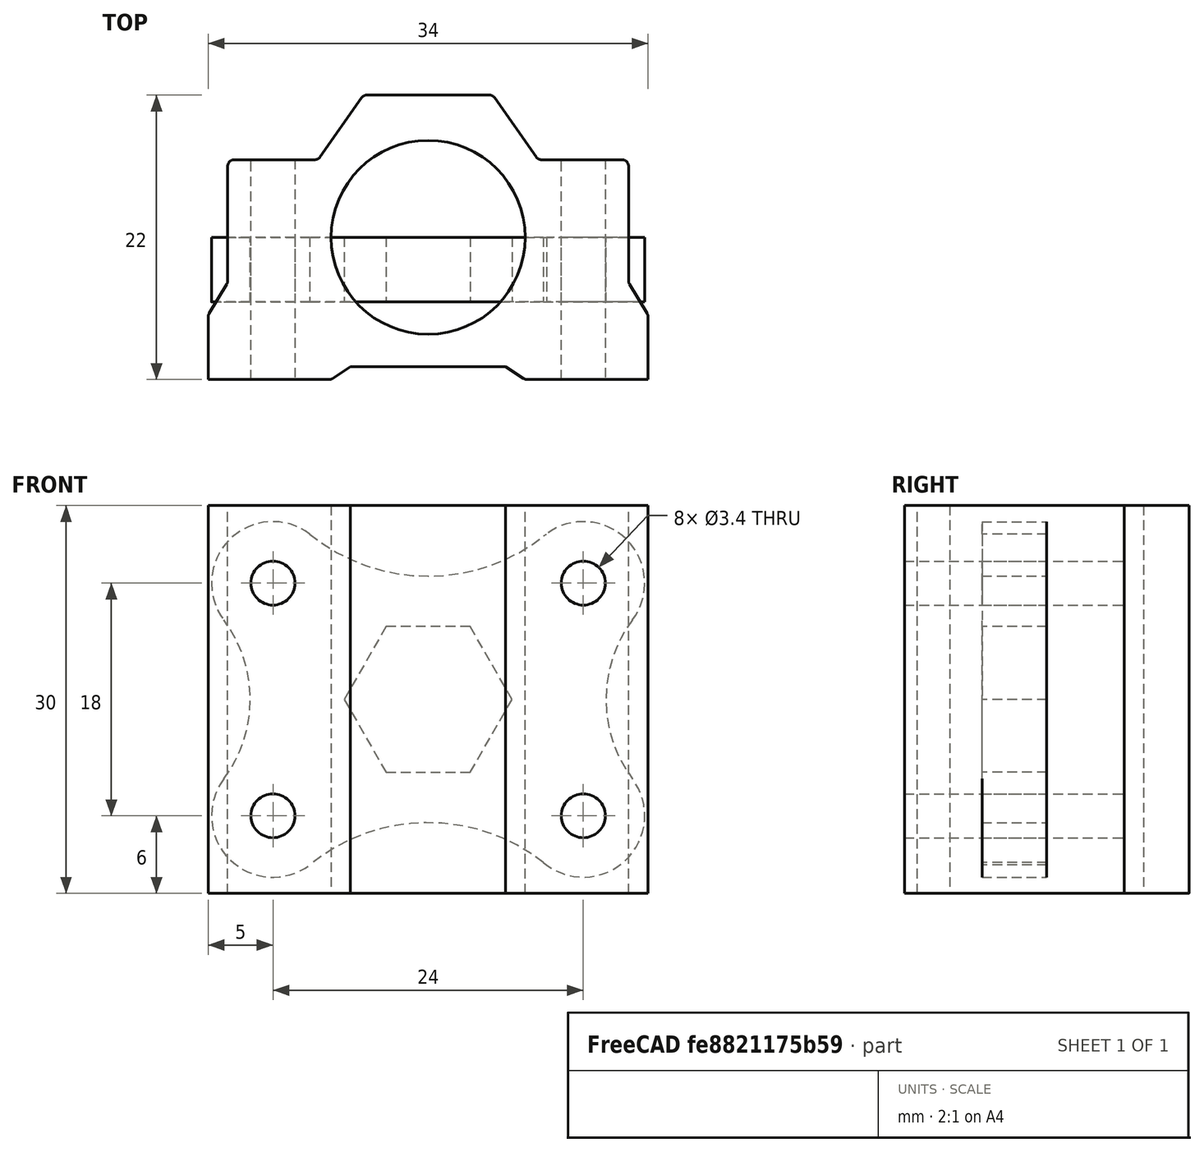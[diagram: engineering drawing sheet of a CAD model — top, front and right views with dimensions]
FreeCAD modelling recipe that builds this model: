
FCSTD DOCUMENT  (FreeCAD 0.19R21938 (Git))
Label: pillow-block-spacer
License: All rights reserved
LicenseURL: http://en.wikipedia.org/wiki/All_rights_reserved
objects: Part::Feature×1, Sketcher::SketchObject×1, PartDesign::Pad×1, PartDesign::Body×1
note: 5 computed .brp shape members not serialized (recipe doc carries the construction recipe); baked Part::Feature solids carry a one-line shape summary decoded from their .brp

FEATURE [Part::Feature] pillow_block_cs8uu
  Placement = pos=(0,0,-15) rot=(0,0,1;0rad)
  shape: bbox 34 x 22 x 30 mm, 37 faces (baked)
FEATURE [Sketcher::SketchObject] Sketch
  MapMode = 5
  Placement = pos=(0,0,0) rot=(1,0,0;1.5708rad)
  Support = -> [XZ_Plane]
  sketch-geometry (19):
    g0: Circle CenterX=-12 CenterY=9 CenterZ=0 NormalX=0 NormalY=0 NormalZ=1 AngleXU=0 Radius=1.7
    g1: Circle CenterX=12 CenterY=9 CenterZ=0 NormalX=0 NormalY=0 NormalZ=1 AngleXU=0 Radius=1.7
    g2: Circle CenterX=12 CenterY=-9 CenterZ=0 NormalX=0 NormalY=0 NormalZ=1 AngleXU=0 Radius=1.7
    g3: Circle CenterX=-12 CenterY=-9 CenterZ=0 NormalX=0 NormalY=0 NormalZ=1 AngleXU=0 Radius=1.7
    g4: ArcOfCircle CenterX=-12 CenterY=9 CenterZ=0 NormalX=0 NormalY=0 NormalZ=1 AngleXU=0 Radius=4.75 StartAngle=0.927295 EndAngle=3.78509
    g5: ArcOfCircle CenterX=12 CenterY=9 CenterZ=0 NormalX=0 NormalY=0 NormalZ=1 AngleXU=0 Radius=4.75 StartAngle=5.63968 EndAngle=8.49748
    g6: ArcOfCircle CenterX=-12 CenterY=-9 CenterZ=0 NormalX=0 NormalY=0 NormalZ=1 AngleXU=0 Radius=4.75 StartAngle=2.49809 EndAngle=5.35589
    g7: ArcOfCircle CenterX=12 CenterY=-9 CenterZ=0 NormalX=0 NormalY=0 NormalZ=1 AngleXU=0 Radius=4.75 StartAngle=4.00641 EndAngle=6.92669
    g8: ArcOfCircle CenterX=-24 CenterY=0 CenterZ=0 NormalX=0 NormalY=0 NormalZ=1 AngleXU=0 Radius=10.25 StartAngle=5.63968 EndAngle=6.92669
    g9: ArcOfCircle CenterX=24 CenterY=0 CenterZ=0 NormalX=0 NormalY=0 NormalZ=1 AngleXU=0 Radius=10.25 StartAngle=2.49809 EndAngle=3.78509
    g10: ArcOfCircle CenterX=0 CenterY=24 CenterZ=0 NormalX=0 NormalY=0 NormalZ=1 AngleXU=0 Radius=14.4625 StartAngle=4.02739 EndAngle=5.39739
    g11: ArcOfCircle CenterX=0 CenterY=-24 CenterZ=0 NormalX=0 NormalY=0 NormalZ=1 AngleXU=0 Radius=14.4625 StartAngle=0.906314 EndAngle=2.2558
    g12: LineSegment StartX=6.5 StartY=0 StartZ=0 EndX=3.25 EndY=5.62917 EndZ=0
    g13: LineSegment StartX=3.25 StartY=5.62917 StartZ=0 EndX=-3.25 EndY=5.62917 EndZ=0
    g14: LineSegment StartX=-3.25 StartY=5.62917 StartZ=0 EndX=-6.5 EndY=9e-16 EndZ=0
    g15: LineSegment StartX=-6.5 StartY=9e-16 StartZ=0 EndX=-3.25 EndY=-5.62917 EndZ=0
    g16: LineSegment StartX=-3.25 StartY=-5.62917 StartZ=0 EndX=3.25 EndY=-5.62917 EndZ=0
    g17: LineSegment StartX=3.25 StartY=-5.62917 StartZ=0 EndX=6.5 EndY=0 EndZ=0
    g18: Circle [constr] CenterX=0 CenterY=0 CenterZ=0 NormalX=0 NormalY=0 NormalZ=1 AngleXU=0 Radius=6.5
  constraints (56):
    c: Diameter(g0) = 3.4
    c: Equal(g1,g0)
    c: Equal(g0,g3)
    c: Equal(g3,g2)
    c: DistanceX(g0,g3) = 0
    c: DistanceX(g2,g1) = 0
    c: DistanceY(g1,g0) = 0
    c: DistanceY(g2,g3) = 0
    c: DistanceX(g0,g1) = 24
    c: DistanceY(g2,g1) = 18
    c: DistanceX(g0,g-1) = 12
    c: DistanceY(g-1,g0) = 9
    c: Coincident(g4,g0)
    c: Coincident(g5,g1)
    c: Coincident(g6,g3)
    c: Coincident(g7,g2)
    c: Equal(g5,g4)
    c: Equal(g6,g4)
    c: Equal(g4,g7)
    c: Diameter(g4) = 9.5
    c: PointOnObject(g8,g-1)
    c: PointOnObject(g9,g-1)
    c: DistanceX(g-1,g9) = 24
    c: DistanceX(g8,g-1) = 24
    c: PointOnObject(g10,g-2)
    c: DistanceY(g-1,g10) = 24
    c: PointOnObject(g11,g-2)
    c: DistanceY(g11,g-1) = 24
    c: Coincident(g12,g13)
    c: Coincident(g13,g14)
    c: Coincident(g14,g15)
    c: Coincident(g15,g16)
    c: Coincident(g16,g17)
    c: Coincident(g17,g12)
    c: Equal(g12, g13-g17) x5
    c: PointOnObject(g12,g18)
    c: PointOnObject(g13,g18)
    c: PointOnObject(g14,g18)
    c: PointOnObject(g15,g18)
    c: PointOnObject(g16,g18)
    c: PointOnObject(g17,g18)
    c: Coincident(g18,g-1)
    c: Horizontal(g13)
    c: Diameter(g18) = 13
    c: Coincident(g6,g8)
    c: Coincident(g6,g11)
    c: Coincident(g7,g11)
    c: Coincident(g5,g10)
    c: Coincident(g4,g10)
    c: Coincident(g4,g8)
    c: DistanceX(g4,g0) = 3.8
    c: Coincident(g5,g9)
    c: Coincident(g7,g9)
    c: DistanceX(g1,g5) = 3.8
    c: DistanceY(g1,g5) = 3.8
    c: DistanceY(g6,g3) = 3.8
FEATURE [PartDesign::Pad] Pad
  Length = 5
  Length2 = 100
  Placement = pos=(0,0,0) rot=(1,0,0;1.5708rad)
  Profile = -> Sketch
  Type = 0
FEATURE [PartDesign::Body] Body  label="pillow-block-spacer"
  Group = -> [Sketch,Pad]
  Origin = -> Origin
  Tip = -> Pad
